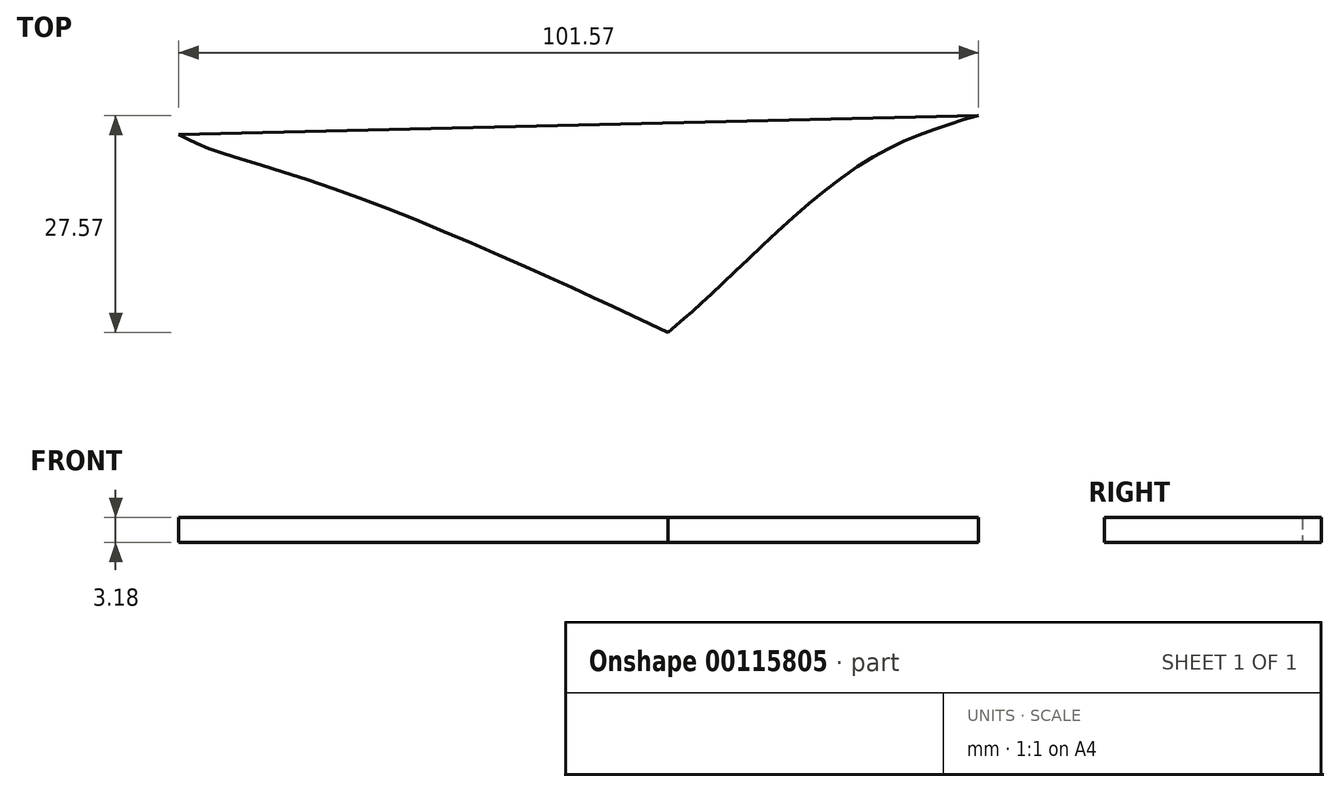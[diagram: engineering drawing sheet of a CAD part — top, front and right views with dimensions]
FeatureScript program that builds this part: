
annotation { "Feature Type Name" : "Feature", "Feature Type Description" : "" }
export const myFeature = defineFeature(function(context is Context, id is Id, definition is map)
    precondition{}
    {
        {
            var Q0;
            Q0=qCreatedBy(makeId("Top.planeOp"),FACE);
            var sketch = newSketch(context, id + "F0", { "sketchPlane" : qUnion([Q0])});
            skFitSpline(sketch, "E0", {"points": [v(-68.76, 6.8) * mm, v(-64.92, 5.06) * mm, v(-49.21, 0) * mm, v(-21.64, -11.34) * mm, v(-6.63, -18.32) * mm], "startDerivative": vector(24.6, -12.79) * mm, "endDerivative": vector(52.14, -24.73) * mm});
            skFitSpline(sketch, "E1", {"points": [v(-6.63, -18.32) * mm, v(0, -12.4) * mm, v(17.8, 2.97) * mm, v(32.8, 9.25) * mm], "startDerivative": vector(22.84, 19.6) * mm, "endDerivative": vector(42.98, 12.67) * mm});
            skLineSegment(sketch, "E2", {"start": v(-68.76, 6.8) * mm, "end": v(32.8, 9.25) * mm});
            skSolve(sketch);
        }
        {
            var Q0;
            Q0=makeQuery(id+"F0.imprint","IMPRINT",FACE,{"disambiguationData":[TD([[makeQuery(id+"F0.imprint","IMPRINT",EDGE,{"derivedFrom":sQuery(id+"F0.wireOp",EDGE,"E0")}),1.0]])]});
            extrude(context, id + "F1", {"entities" : qUnion([Q0]), "depth" : 3.17 * mm});
        }
    });
